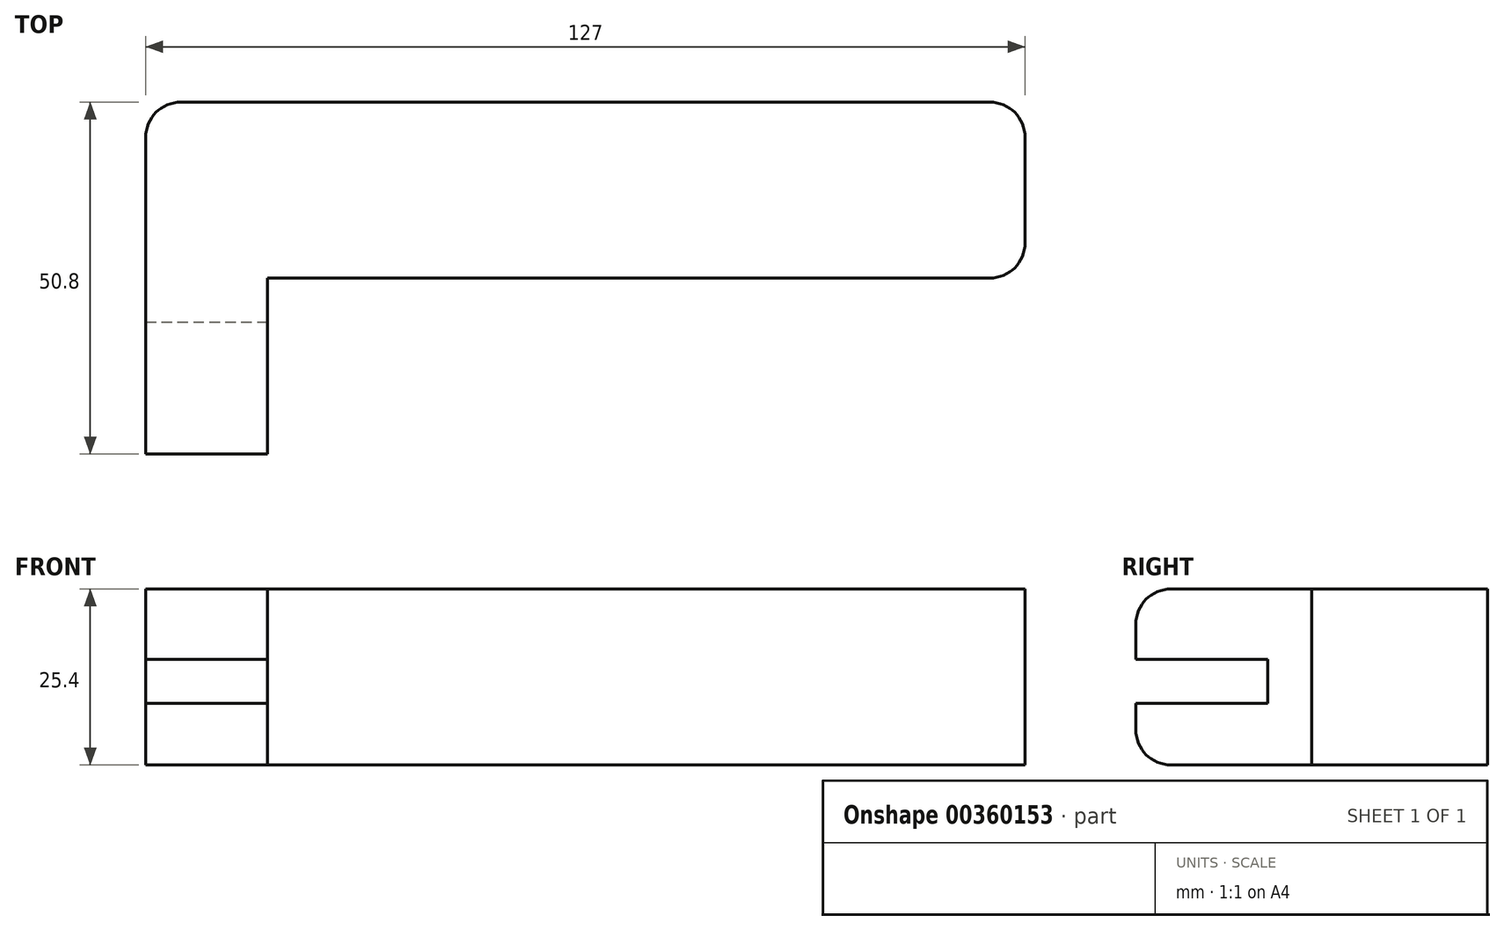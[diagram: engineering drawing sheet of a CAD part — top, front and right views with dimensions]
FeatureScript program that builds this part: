
annotation { "Feature Type Name" : "Feature", "Feature Type Description" : "" }
export const myFeature = defineFeature(function(context is Context, id is Id, definition is map)
    precondition{}
    {
        {
            var Q0;
            Q0=qCreatedBy(makeId("Front.planeOp"),FACE);
            var sketch = newSketch(context, id + "F0", { "sketchPlane" : qUnion([Q0])});
            skLineSegment(sketch, "E0.bottom", {"start": v(0, 0) * mm, "end": v(127, 0) * mm});
            skLineSegment(sketch, "E0.top", {"start": v(0, 25.4) * mm, "end": v(127, 25.4) * mm});
            skLineSegment(sketch, "E0.left", {"start": v(0, 0) * mm, "end": v(0, 25.4) * mm});
            skLineSegment(sketch, "E0.right", {"start": v(127, 0) * mm, "end": v(127, 25.4) * mm});
            skSolve(sketch);
        }
        {
            var Q0;
            Q0=makeQuery(id+"F0.imprint","IMPRINT",FACE,{"disambiguationData":[TD([[makeQuery(id+"F0.imprint","IMPRINT",EDGE,{"derivedFrom":sQuery(id+"F0.wireOp",EDGE,"E0.bottom")}),1.0]])]});
            extrude(context, id + "F1", {"entities" : qUnion([Q0]), "oppositeDirection" : true, "depth" : 25.4 * mm});
        }
        {
            var Q0;
            Q0=makeQuery(id+"F1.opExtrude","CAP_FACE",FACE,{"disambiguationData":[OSD([sQuery(id+"F0.wireOp",EDGE,"E0.bottom"),sQuery(id+"F0.wireOp",EDGE,"E0.top"),sQuery(id+"F0.wireOp",EDGE,"E0.left"),sQuery(id+"F0.wireOp",EDGE,"E0.right")])],"isStart":true});
            var sketch = newSketch(context, id + "F2", { "sketchPlane" : qUnion([Q0])});
            skLineSegment(sketch, "E1.bottom", {"start": v(0, 0) * mm, "end": v(17.6, 0) * mm});
            skLineSegment(sketch, "E1.top", {"start": v(0, 25.4) * mm, "end": v(17.6, 25.4) * mm});
            skLineSegment(sketch, "E1.left", {"start": v(0, 0) * mm, "end": v(0, 25.4) * mm});
            skLineSegment(sketch, "E1.right", {"start": v(17.6, 0) * mm, "end": v(17.6, 25.4) * mm});
            skSolve(sketch);
        }
        {
            var Q0;
            Q0=makeQuery(id+"F2.imprint","IMPRINT",FACE,{"disambiguationData":[TD([[makeQuery(id+"F2.imprint","IMPRINT",EDGE,{"derivedFrom":sQuery(id+"F2.wireOp",EDGE,"E1.bottom")}),1.0]])]});
            extrude(context, id + "F3", {"entities" : qUnion([Q0]), "operationType" : NewBodyOperationType.ADD, "depth" : 25.4 * mm});
        }
        {
            var Q0;
            Q0=makeQuery(id+"F3.opExtrude","CAP_FACE",FACE,{"disambiguationData":[OSD([sQuery(id+"F2.wireOp",EDGE,"E1.bottom"),sQuery(id+"F2.wireOp",EDGE,"E1.top"),sQuery(id+"F2.wireOp",EDGE,"E1.left"),sQuery(id+"F2.wireOp",EDGE,"E1.right")])],"isStart":false});
            var sketch = newSketch(context, id + "F4", { "sketchPlane" : qUnion([Q0])});
            skLineSegment(sketch, "E2.bottom", {"start": v(0, 15.25) * mm, "end": v(17.6, 15.25) * mm});
            skLineSegment(sketch, "E2.top", {"start": v(0, 8.9) * mm, "end": v(17.6, 8.9) * mm});
            skLineSegment(sketch, "E2.left", {"start": v(0, 15.25) * mm, "end": v(0, 8.9) * mm});
            skLineSegment(sketch, "E2.right", {"start": v(17.6, 15.25) * mm, "end": v(17.6, 8.9) * mm});
            skSolve(sketch);
        }
        {
            var Q0;
            Q0=makeQuery(id+"F4.imprint","IMPRINT",FACE,{"disambiguationData":[TD([[makeQuery(id+"F4.imprint","IMPRINT",EDGE,{"derivedFrom":sQuery(id+"F4.wireOp",EDGE,"E2.bottom")}),-1.0]])]});
            extrude(context, id + "F5", {"entities" : qUnion([Q0]), "operationType" : NewBodyOperationType.REMOVE, "oppositeDirection" : true, "depth" : 19.05 * mm});
        }
        {
            var Q0;
            Q0=makeQuery(id+"F3.opExtrude","CAP_EDGE",EDGE,{"disambiguationData":[OSD([sQuery(id+"F2.wireOp",EDGE,"E1.top")])],"isStart":false});
            var Q1;
            Q1=makeQuery(id+"F3.opExtrude","CAP_EDGE",EDGE,{"disambiguationData":[OSD([sQuery(id+"F2.wireOp",EDGE,"E1.bottom")])],"isStart":false});
            var Q2;
            Q2=makeQuery(id+"F1.opExtrude","CAP_EDGE",EDGE,{"disambiguationData":[OSD([sQuery(id+"F0.wireOp",EDGE,"E0.right")])],"isStart":true});
            var Q3;
            Q3=makeQuery(id+"F1.opExtrude","CAP_EDGE",EDGE,{"disambiguationData":[OSD([sQuery(id+"F0.wireOp",EDGE,"E0.right")])],"isStart":false});
            fillet(context, id + "F6", {"entities" : qUnion([Q0, Q1, Q2, Q3]), "radius" : 5.08 * mm, "tangentPropagation" : true, "allowEdgeOverflow" : false});
        }
        {
            var Q0;
            Q0=makeQuery(id+"F1.opExtrude","CAP_EDGE",EDGE,{"disambiguationData":[OSD([sQuery(id+"F0.wireOp",EDGE,"E0.left")])],"isStart":false});
            fillet(context, id + "F7", {"entities" : qUnion([Q0]), "radius" : 5.08 * mm, "tangentPropagation" : true, "allowEdgeOverflow" : false});
        }
    });
